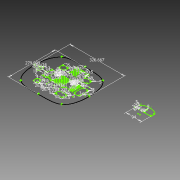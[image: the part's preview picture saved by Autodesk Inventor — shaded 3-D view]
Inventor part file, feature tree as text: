
AUTODESK INVENTOR PART (.ipt)
format: ipt  version: 2012 (Build 160160000, 160)  size: 219,136 bytes
history: native  units: mm
features: sketch x1
ambient origin geometry x8: Origin, YZ Plane, XZ Plane, XY Plane, X Axis, Y Axis, Z Axis, Center Point
feature tree (1):
  sketch  "Sketch1"  dims[d51=3.0mm d54=3.0mm d64=3.0mm d69=3.0mm d76=3.0mm d77=3.0mm d78=51.0mm d82=51.0mm d91=25.0mm d94=51.0mm d96=51.0mm d116=64.0mm d117=3.0mm d118=3.0mm d119=3.0mm d120=3.0mm d122=5.632993mm d125=4.7mm d126=5.0mm d128=10.0mm d129=5.0mm d131=5.0mm d132=66.0mm d134=3.0mm d135=3.0mm d137=3.0mm d138=5.682993mm d139=4.7mm d140=5.0mm d141=10.0mm d142=5.0mm d143=3.0mm d144=5.0mm d145=5.0mm d150=3.0mm d160=36.2mm d162=50.0mm d163=5.0mm d164=40.0mm d165=28.5mm d166=5.0mm d170=5.0mm d171=35.0mm d172=5.0mm d177=66.0mm d184=3.0mm d185=10.0mm d186=25.0mm d187=3.0mm d188=25.0mm d189=10.0mm d190=3.0mm d196=3.0mm d197=3.0mm d198=30.0mm d199=60.0mm d200=10.0mm d201=35.0mm d202=3.0mm d203=30.0mm d204=34.23504mm d205=34.23504mm d206=35.0mm d207=30.0mm d208=31.5mm d209=31.5mm d210=50.55mm d213=5.554212mm d215=5.0mm d216=5.554212mm d217=5.117007mm d219=5.0mm d220=5.0mm d221=5.117007mm d232=14.0mm d236=2.0mm d238=13.0mm d239=3.0mm d244=3.0mm d245=26.4mm d246=22.0mm d247=8.0mm d248=3.0mm d249=3.0mm d250=26.4mm d251=22.0mm d252=16.0mm d253=16.0mm d271=30.0mm d274=28.5mm d275=5.0mm d276=279.999493mm d277=326.667217mm d278=20.5mm d279=5.0mm d280=17.0mm d282=60.0mm d283=5.0mm d284=5.0mm d285=5.0mm d286=94.0mm d288=25.0mm d289=5.0mm d291=3.0mm d292=4.0mm d293=4.0mm d294=49.0mm d295=8.0mm d296=20.0mm]
